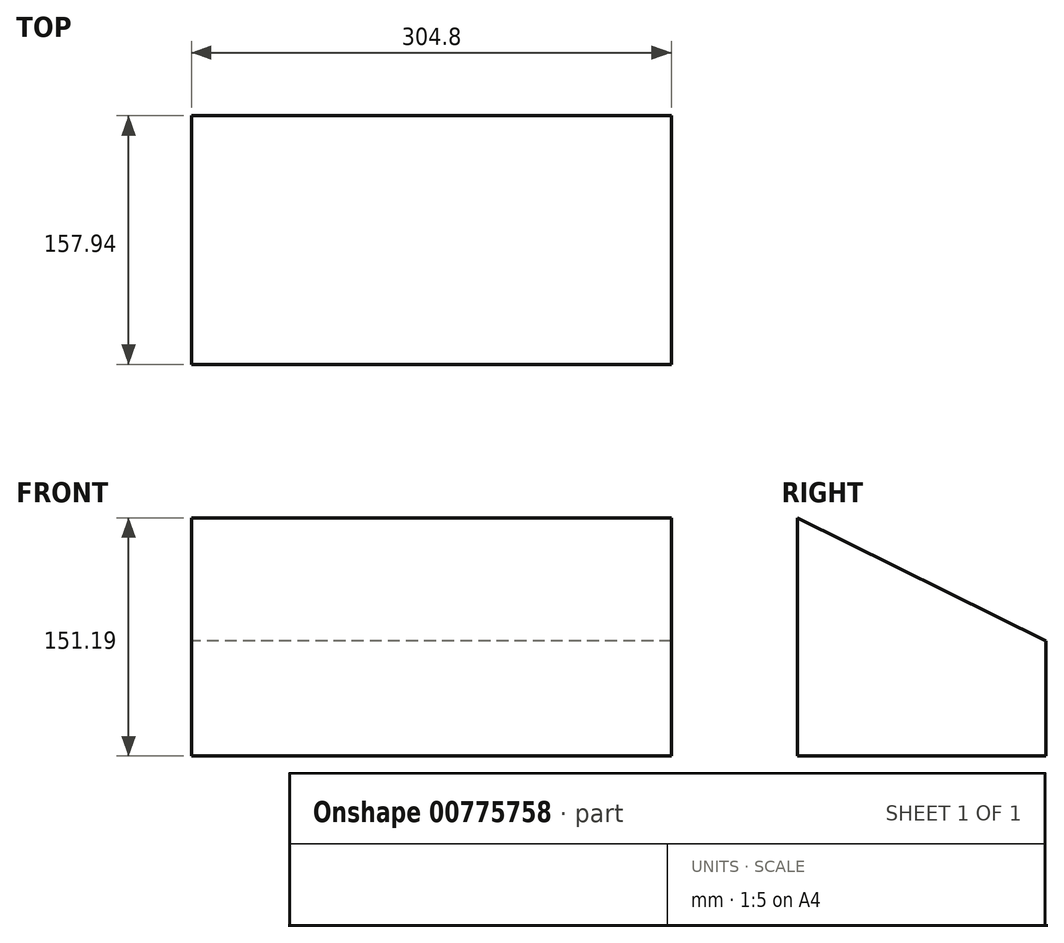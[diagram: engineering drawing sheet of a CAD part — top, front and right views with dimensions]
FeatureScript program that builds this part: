
annotation { "Feature Type Name" : "Feature", "Feature Type Description" : "" }
export const myFeature = defineFeature(function(context is Context, id is Id, definition is map)
    precondition{}
    {
        {
            var Q0;
            Q0=qCreatedBy(makeId("Right.planeOp"),FACE);
            var sketch = newSketch(context, id + "F0", { "sketchPlane" : qUnion([Q0])});
            skLineSegment(sketch, "E0", {"start": v(-51.09, 0) * mm, "end": v(106.85, 0) * mm});
            skLineSegment(sketch, "E1", {"start": v(106.85, 72.85) * mm, "end": v(-51.09, 151.2) * mm});
            skLineSegment(sketch, "E2", {"start": v(-51.09, 151.2) * mm, "end": v(-51.09, 0) * mm});
            skLineSegment(sketch, "E3", {"start": v(106.85, 72.85) * mm, "end": v(106.85, 0) * mm});
            skSolve(sketch);
        }
        {
            var Q0;
            Q0 = qSketchRegion(id + "F0", true);
            extrude(context, id + "F1", {"entities" : qUnion([Q0]), "depth" : 304.8 * mm, "offsetDistance" : 25.4 * mm});
        }
    });
